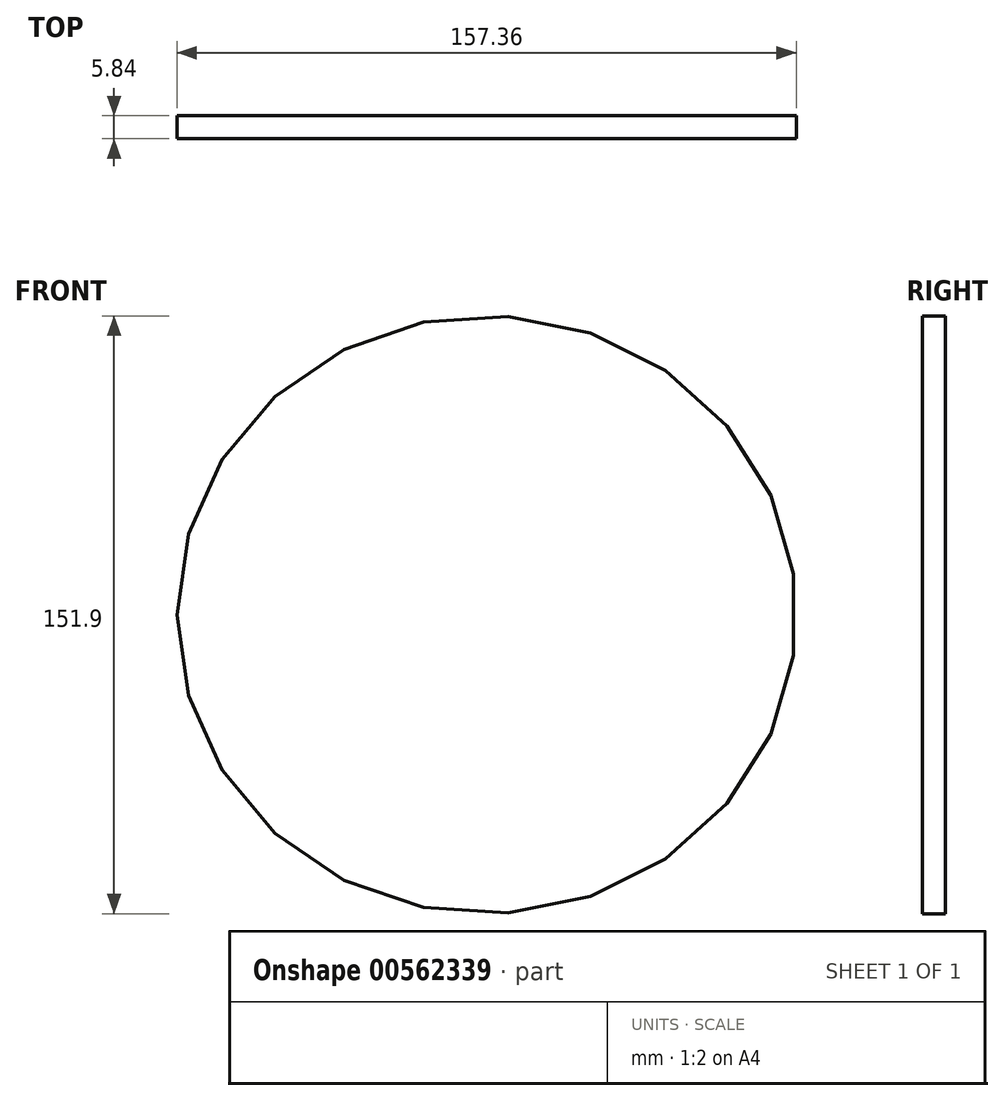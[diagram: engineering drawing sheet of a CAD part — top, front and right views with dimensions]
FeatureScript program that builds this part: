
annotation { "Feature Type Name" : "Feature", "Feature Type Description" : "" }
export const myFeature = defineFeature(function(context is Context, id is Id, definition is map)
    precondition{}
    {
        {
            var Q0;
            Q0=qCreatedBy(makeId("Front.planeOp"),FACE);
            var sketch = newSketch(context, id + "F0", { "sketchPlane" : qUnion([Q0])});
            skEllipse(sketch, "E0", {"center": v(0, 0) * mm, "majorRadius": 75.95 * mm, "minorRadius": 78.68 * mm, "majorAxis": v(0, 1)});
            skSolve(sketch);
        }
        {
            var Q0;
            Q0 = qSketchRegion(id + "F0", true);
            extrude(context, id + "F1", {"entities" : qUnion([Q0]), "depth" : 5.84 * mm, "offsetDistance" : 25.4 * mm});
        }
    });
